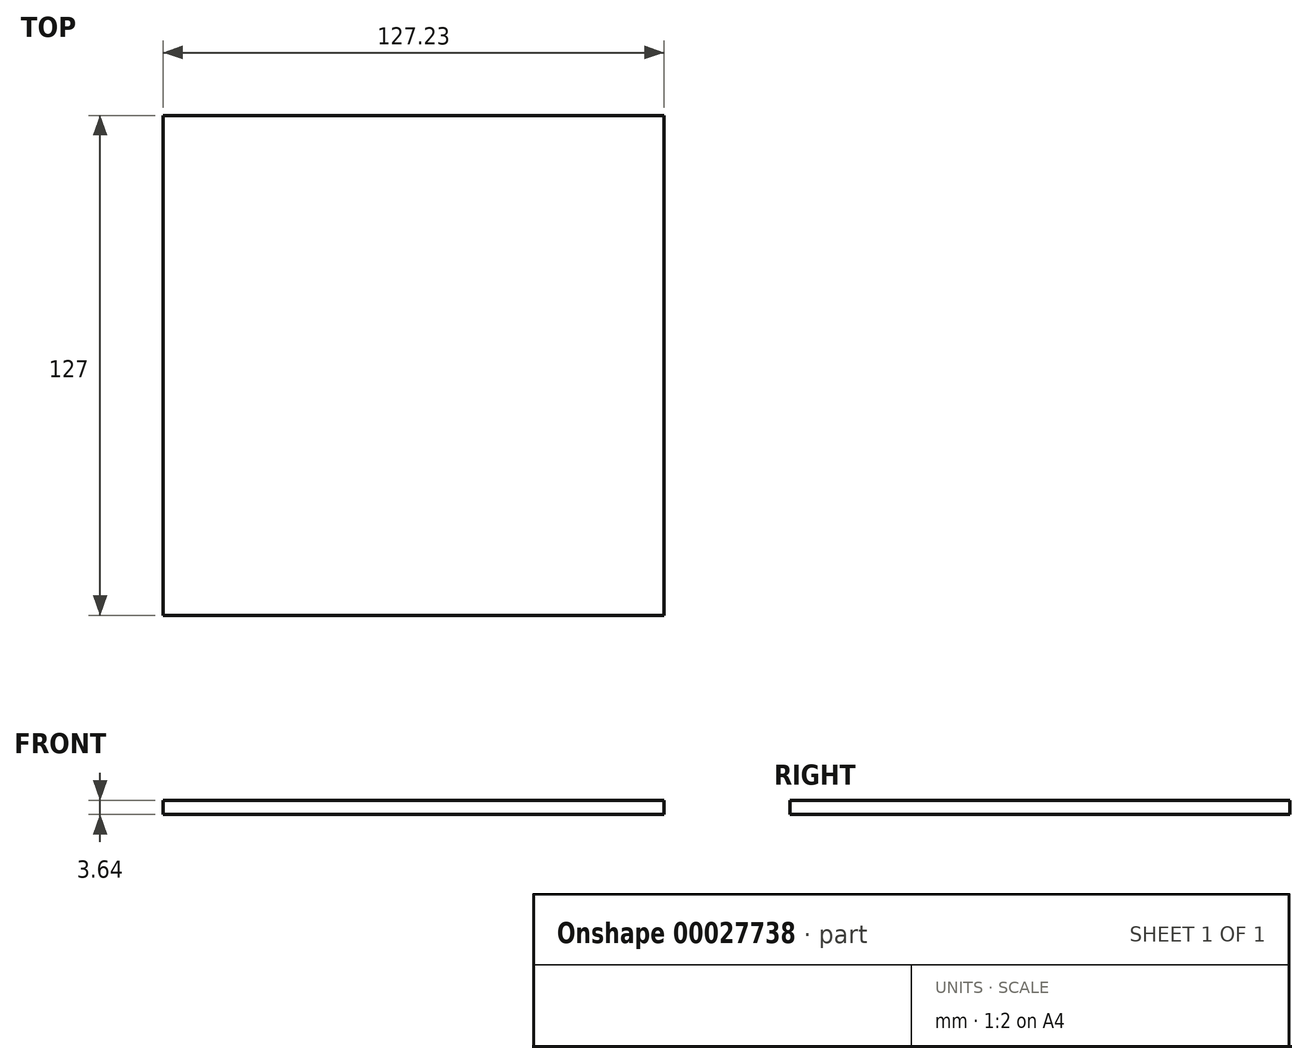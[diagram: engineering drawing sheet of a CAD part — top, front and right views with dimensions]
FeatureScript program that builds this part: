
annotation { "Feature Type Name" : "Feature", "Feature Type Description" : "" }
export const myFeature = defineFeature(function(context is Context, id is Id, definition is map)
    precondition{}
    {
        {
            var Q0;
            Q0=qCreatedBy(makeId("Front.planeOp"),FACE);
            var sketch = newSketch(context, id + "F0", { "sketchPlane" : qUnion([Q0])});
            skLineSegment(sketch, "E0.bottom", {"start": v(-60.73, -13.82) * mm, "end": v(66.5, -13.82) * mm});
            skLineSegment(sketch, "E0.top", {"start": v(-60.73, -17.46) * mm, "end": v(66.5, -17.46) * mm});
            skLineSegment(sketch, "E0.left", {"start": v(-60.73, -13.82) * mm, "end": v(-60.73, -17.46) * mm});
            skLineSegment(sketch, "E0.right", {"start": v(66.5, -13.82) * mm, "end": v(66.5, -17.46) * mm});
            skSolve(sketch);
        }
        {
            var Q0;
            Q0=makeQuery(id+"F0.imprint","IMPRINT",FACE,{"disambiguationData":[TD([[makeQuery(id+"F0.imprint","IMPRINT",EDGE,{"derivedFrom":sQuery(id+"F0.wireOp",EDGE,"E0.bottom")}),-1.0]])]});
            extrude(context, id + "F1", {"entities" : qUnion([Q0]), "depth" : 127 * mm});
        }
    });
